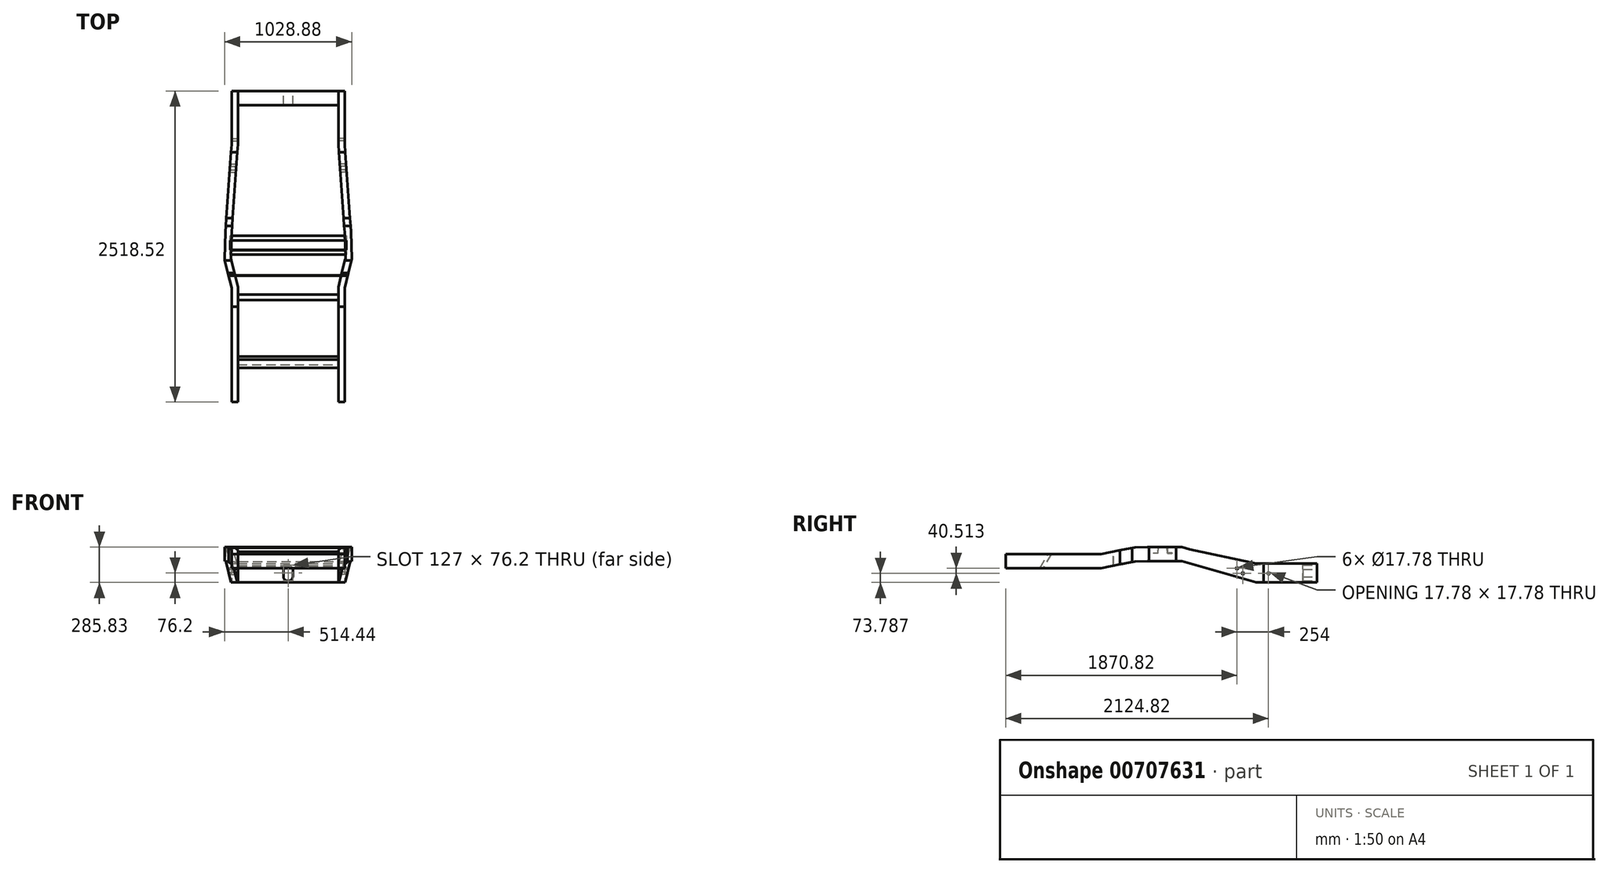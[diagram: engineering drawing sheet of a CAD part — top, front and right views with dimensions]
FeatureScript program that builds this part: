
annotation { "Feature Type Name" : "Feature", "Feature Type Description" : "" }
export const myFeature = defineFeature(function(context is Context, id is Id, definition is map)
    precondition{}
    {
        {
            var Q0;
            Q0=qCreatedBy(makeId("Top.planeOp"),FACE);
            var sketch = newSketch(context, id + "F0", { "sketchPlane" : qUnion([Q0])});
            skLineSegment(sketch, "E0", {"start": v(0, 1936.1) * mm, "end": v(0, -5906.31) * mm, "construction": true});
            skLineSegment(sketch, "E1", {"start": v(431.8, 0) * mm, "end": v(431.8, -431.8) * mm});
            skLineSegment(sketch, "E2", {"start": v(431.8, -431.8) * mm, "end": v(482.6, -1141.18) * mm});
            skLineSegment(sketch, "E3", {"start": v(482.6, -1141.18) * mm, "end": v(488.95, -1356.99) * mm});
            skLineSegment(sketch, "E4", {"start": v(488.95, -1356.99) * mm, "end": v(431.8, -1591.42) * mm});
            skLineSegment(sketch, "E5", {"start": v(431.8, -1591.42) * mm, "end": v(431.8, -2518.52) * mm});
            skLineSegment(sketch, "E6", {"start": v(431.8, -431.8) * mm, "end": v(431.8, -1285.92) * mm, "construction": true});
            skSolve(sketch);
        }
        {
            var Q0;
            Q0=qCreatedBy(makeId("Front.planeOp"),FACE);
            var Q1;
            Q1=sQuery(id+"F0.wireOp",VERTEX,"E1.start");
            cPlane(context, id + "F1", {"entities" : qUnion([Q0, Q1]), "cplaneType" : CPlaneType.PLANE_POINT, "offset" : 25.4 * mm, "width" : 152.4 * mm, "height" : 152.4 * mm});
        }
        {
            var Q0;
            Q0=qCreatedBy(id+"F1.planeOp",FACE);
            var sketch = newSketch(context, id + "F2", { "sketchPlane" : qUnion([Q0])});
            skLineSegment(sketch, "E7.bottom", {"start": v(406.4, 203.2) * mm, "end": v(457.2, 203.2) * mm});
            skLineSegment(sketch, "E7.top", {"start": v(406.4, -203.2) * mm, "end": v(457.2, -203.2) * mm});
            skLineSegment(sketch, "E7.left", {"start": v(406.4, 203.2) * mm, "end": v(406.4, -203.2) * mm});
            skLineSegment(sketch, "E7.right", {"start": v(457.2, 203.2) * mm, "end": v(457.2, -203.2) * mm});
            skPoint(sketch, "E7.middle", {"position": v(431.8, 0) * mm});
            skLineSegment(sketch, "E8", {"start": v(0, 0) * mm, "end": v(572.75, 0) * mm, "construction": true});
            skSolve(sketch);
        }
        {
            var Q0;
            Q0=qSketchRegion(id+"F2",true);
            var Q1;
            Q1=qConstructionFilter(qBodyType(qCreatedBy(id+"F0",EDGE),BodyType.WIRE),ConstructionObject.NO);
            sweep(context, id + "F3", {"profiles" : qUnion([Q0]), "path" : qUnion([Q1])});
        }
        {
            var Q0;
            Q0=qCreatedBy(makeId("Right.planeOp"),FACE);
            var sketch = newSketch(context, id + "F4", { "sketchPlane" : qUnion([Q0])});
            skLineSegment(sketch, "E9", {"start": v(0, -203.2) * mm, "end": v(-493.71, -203.2) * mm});
            skLineSegment(sketch, "E10", {"start": v(-493.71, -203.2) * mm, "end": v(-1091.9, -31.67) * mm});
            skLineSegment(sketch, "E11", {"start": v(-1091.9, -31.67) * mm, "end": v(-1371.3, -31.67) * mm});
            skLineSegment(sketch, "E12", {"start": v(-1371.3, -31.67) * mm, "end": v(-1472.9, -33.44) * mm});
            skLineSegment(sketch, "E13", {"start": v(-1371.3, -31.67) * mm, "end": v(-1529.34, -31.67) * mm, "construction": true});
            skLineSegment(sketch, "E14", {"start": v(-1472.9, -33.44) * mm, "end": v(-1747.16, -86.76) * mm});
            skLineSegment(sketch, "E15", {"start": v(-1747.16, -86.76) * mm, "end": v(-2518.52, -86.76) * mm});
            skLineSegment(sketch, "E16", {"start": v(-2518.52, -86.76) * mm, "end": v(-2518.52, -253.61) * mm});
            skLineSegment(sketch, "E17", {"start": v(-2518.52, -253.61) * mm, "end": v(0, -269.23) * mm});
            skLineSegment(sketch, "E18", {"start": v(0, -269.23) * mm, "end": v(0, -203.2) * mm});
            skLineSegment(sketch, "E19", {"start": v(0, -50.8) * mm, "end": v(-493.71, -50.8) * mm});
            skLineSegment(sketch, "E20", {"start": v(-493.71, -50.8) * mm, "end": v(-1028.7, 64.5) * mm});
            skLineSegment(sketch, "E21", {"start": v(-1028.7, 64.5) * mm, "end": v(-1028.7, -49.8) * mm, "construction": true});
            skLineSegment(sketch, "E22", {"start": v(-1091.9, -31.67) * mm, "end": v(-1091.9, 82.63) * mm, "construction": true});
            skLineSegment(sketch, "E23", {"start": v(-1371.3, -31.67) * mm, "end": v(-1371.3, 82.63) * mm, "construction": true});
            skLineSegment(sketch, "E24", {"start": v(-1472.9, -33.44) * mm, "end": v(-1472.9, 80.86) * mm, "construction": true});
            skLineSegment(sketch, "E25", {"start": v(-1747.16, -86.76) * mm, "end": v(-1747.16, 27.54) * mm, "construction": true});
            skLineSegment(sketch, "E26", {"start": v(-1028.7, 64.5) * mm, "end": v(-1091.9, 82.63) * mm});
            skLineSegment(sketch, "E27", {"start": v(-1091.9, 82.63) * mm, "end": v(-1371.3, 82.63) * mm});
            skLineSegment(sketch, "E28", {"start": v(-1472.9, 80.86) * mm, "end": v(-1747.16, 27.54) * mm});
            skLineSegment(sketch, "E29", {"start": v(-1472.9, 80.86) * mm, "end": v(-1371.3, 82.63) * mm});
            skLineSegment(sketch, "E30", {"start": v(-2518.52, -86.76) * mm, "end": v(-2518.52, 27.54) * mm, "construction": true});
            skLineSegment(sketch, "E31", {"start": v(-1747.16, 27.54) * mm, "end": v(-2518.52, 27.54) * mm});
            skLineSegment(sketch, "E32", {"start": v(-2518.52, 27.54) * mm, "end": v(-2518.52, 524.74) * mm});
            skLineSegment(sketch, "E33", {"start": v(-2518.52, 524.74) * mm, "end": v(0, 524.74) * mm});
            skLineSegment(sketch, "E34", {"start": v(0, 524.74) * mm, "end": v(0, -50.8) * mm});
            skSolve(sketch);
        }
        {
            var Q0;
            Q0=qSketchRegion(id+"F4",true);
            var Q1;
            Q1=makeQuery(id+"F3.opSweep","SWEPT_FACE",FACE,{"disambiguationData":[OSD([sQuery(id+"F0.wireOp",EDGE,"1umSsKEu-dJId-BIwL-yde3-wRK5SwyTBX2N"),sQuery(id+"F2.wireOp",EDGE,"E7.right")])]});
            extrude(context, id + "F5", {"entities" : qUnion([Q0]), "operationType" : NewBodyOperationType.REMOVE, "depth" : 609.6 * mm, "endBoundEntityFace" : qUnion([Q1]), "offsetDistance" : 25.4 * mm});
        }
        {
            var Q0;
            Q0=makeQuery(id+"F3.opSweep","SWEPT_FACE",FACE,{"disambiguationData":[OSD([sQuery(id+"F0.wireOp",EDGE,"E1"),sQuery(id+"F2.wireOp",EDGE,"E7.left")])]});
            var sketch = newSketch(context, id + "F6", { "sketchPlane" : qUnion([Q0])});
            skLineSegment(sketch, "E35", {"start": v(-416.37, -129.41) * mm, "end": v(600.08, -129.41) * mm, "construction": true});
            skLineSegment(sketch, "E36", {"start": v(393.7, 39.46) * mm, "end": v(393.7, -270.74) * mm, "construction": true});
            skLineSegment(sketch, "E37", {"start": v(393.7, -88.9) * mm, "end": v(863.06, -88.9) * mm, "construction": true});
            skLineSegment(sketch, "E38", {"start": v(600.08, 71) * mm, "end": v(600.08, -269.25) * mm, "construction": true});
            skLineSegment(sketch, "E39", {"start": v(647.7, 77.42) * mm, "end": v(647.7, -282.1) * mm, "construction": true});
            skCircle(sketch, "E40", {"center": v(600.08, -129.41) * mm, "radius": 8.9 * mm});
            skCircle(sketch, "E41", {"center": v(647.7, -88.9) * mm, "radius": 8.9 * mm});
            skCircle(sketch, "E42", {"center": v(393.7, -129.41) * mm, "radius": 8.9 * mm});
            skSolve(sketch);
        }
        {
            var Q0;
            Q0=qSketchRegion(id+"F6",true);
            extrude(context, id + "F7", {"entities" : qUnion([Q0]), "operationType" : NewBodyOperationType.REMOVE, "endBound" : BoundingType.SYMMETRIC, "oppositeDirection" : true, "depth" : 508 * mm, "offsetDistance" : 25.4 * mm});
        }
        {
            var Q0;
            Q0=makeQuery(id+"F3.opSweep","SWEPT_BODY",BODY,{"disambiguationData":[OSD([sQuery(id+"F0.wireOp",EDGE,"zRG0IsD7-SMmf-8p0A-3XBu-xbHUB45AKsED"),sQuery(id+"F2.wireOp",EDGE,"E7.bottom"),sQuery(id+"F2.wireOp",EDGE,"E7.top"),sQuery(id+"F2.wireOp",EDGE,"E7.left"),sQuery(id+"F2.wireOp",EDGE,"E7.right")])]});
            var Q1;
            Q1=qCreatedBy(makeId("Right.planeOp"),FACE);
            mirror(context, id + "F8", {"entities" : qUnion([Q0]), "mirrorPlane" : qUnion([Q1])});
        }
        {
            var Q0;
            Q0=makeQuery(id+"F3.opSweep","SWEPT_FACE",FACE,{"disambiguationData":[OSD([sQuery(id+"F0.wireOp",EDGE,"E1"),sQuery(id+"F2.wireOp",EDGE,"E7.left")])]});
            var sketch = newSketch(context, id + "F9", { "sketchPlane" : qUnion([Q0])});
            skLineSegment(sketch, "E43.bottom", {"start": v(0, -50.8) * mm, "end": v(114.3, -50.8) * mm});
            skLineSegment(sketch, "E43.top", {"start": v(0, -203.2) * mm, "end": v(114.3, -203.2) * mm});
            skLineSegment(sketch, "E43.left", {"start": v(0, -50.8) * mm, "end": v(0, -203.2) * mm});
            skLineSegment(sketch, "E43.right", {"start": v(114.3, -50.8) * mm, "end": v(114.3, -203.2) * mm});
            skSolve(sketch);
        }
        {
            var Q0;
            Q0=qSketchRegion(id+"F9",true);
            var Q1;
            Q1=makeQuery(id+"F8.opPattern","COPY",FACE,{"derivedFrom":makeQuery(id+"F3.opSweep","SWEPT_FACE",FACE,{"disambiguationData":[OSD([sQuery(id+"F0.wireOp",EDGE,"E1"),sQuery(id+"F2.wireOp",EDGE,"E7.left")])]}),"instanceName":"1"});
            extrude(context, id + "F10", {"entities" : qUnion([Q0]), "endBound" : BoundingType.UP_TO_SURFACE, "depth" : 25.4 * mm, "endBoundEntityFace" : qUnion([Q1]), "offsetDistance" : 25.4 * mm});
        }
        {
            var Q0;
            Q0=makeQuery(id+"F3.opSweep","SWEPT_FACE",FACE,{"disambiguationData":[OSD([sQuery(id+"F0.wireOp",EDGE,"E5"),sQuery(id+"F2.wireOp",EDGE,"E7.left")])]});
            var sketch = newSketch(context, id + "F11", { "sketchPlane" : qUnion([Q0])});
            skLineSegment(sketch, "E44", {"start": v(2175.62, 27.54) * mm, "end": v(2241.62, -86.76) * mm});
            skLineSegment(sketch, "E45", {"start": v(2241.62, -86.76) * mm, "end": v(2216.22, -86.76) * mm});
            skLineSegment(sketch, "E46", {"start": v(2216.22, -86.76) * mm, "end": v(2150.22, 27.54) * mm});
            skLineSegment(sketch, "E47", {"start": v(2150.22, 27.54) * mm, "end": v(2175.62, 27.54) * mm});
            skSolve(sketch);
        }
        {
            var Q0;
            Q0=qSketchRegion(id+"F11",true);
            var Q1;
            Q1=makeQuery(id+"F8.opPattern","COPY",FACE,{"derivedFrom":makeQuery(id+"F3.opSweep","SWEPT_FACE",FACE,{"disambiguationData":[OSD([sQuery(id+"F0.wireOp",EDGE,"E5"),sQuery(id+"F2.wireOp",EDGE,"E7.left")])]}),"instanceName":"1"});
            extrude(context, id + "F12", {"entities" : qUnion([Q0]), "endBound" : BoundingType.UP_TO_SURFACE, "depth" : 25.4 * mm, "endBoundEntityFace" : qUnion([Q1]), "offsetDistance" : 25.4 * mm});
        }
        {
            var Q0;
            Q0=makeQuery(id+"F3.opSweep","SWEPT_FACE",FACE,{"disambiguationData":[OSD([sQuery(id+"F0.wireOp",EDGE,"E5"),sQuery(id+"F2.wireOp",EDGE,"E7.left")])]});
            var sketch = newSketch(context, id + "F13", { "sketchPlane" : qUnion([Q0])});
            skLineSegment(sketch, "E48", {"start": v(1693.02, 38.07) * mm, "end": v(1646.27, 47.15) * mm});
            skLineSegment(sketch, "E49", {"start": v(1646.27, 47.15) * mm, "end": v(1646.27, -67.15) * mm});
            skLineSegment(sketch, "E50", {"start": v(1646.27, -67.15) * mm, "end": v(1693.02, -76.23) * mm});
            skLineSegment(sketch, "E51", {"start": v(1693.02, -76.23) * mm, "end": v(1693.02, -73.13) * mm});
            skLineSegment(sketch, "E52", {"start": v(1649.32, 43.46) * mm, "end": v(1693.02, 34.96) * mm});
            skLineSegment(sketch, "E53", {"start": v(1693.02, 34.96) * mm, "end": v(1693.02, 38.07) * mm});
            skLineSegment(sketch, "E54", {"start": v(1693.02, -73.13) * mm, "end": v(1649.32, -64.63) * mm});
            skLineSegment(sketch, "E55", {"start": v(1649.32, 43.46) * mm, "end": v(1649.32, -64.63) * mm});
            skSolve(sketch);
        }
        {
            var Q0;
            Q0=qSketchRegion(id+"F13",true);
            var Q1;
            Q1=makeQuery(id+"F8.opPattern","COPY",FACE,{"derivedFrom":makeQuery(id+"F3.opSweep","SWEPT_FACE",FACE,{"disambiguationData":[OSD([sQuery(id+"F0.wireOp",EDGE,"E5"),sQuery(id+"F2.wireOp",EDGE,"E7.left")])]}),"instanceName":"1"});
            extrude(context, id + "F14", {"entities" : qUnion([Q0]), "endBound" : BoundingType.UP_TO_SURFACE, "depth" : 25.4 * mm, "endBoundEntityFace" : qUnion([Q1]), "offsetDistance" : 25.4 * mm});
        }
        {
            var Q0;
            Q0=qCreatedBy(makeId("Right.planeOp"),FACE);
            var sketch = newSketch(context, id + "F15", { "sketchPlane" : qUnion([Q0])});
            skLineSegment(sketch, "E56", {"start": v(-1248.52, 150.62) * mm, "end": v(-1248.52, -76.38) * mm, "construction": true});
            skLineSegment(sketch, "E57", {"start": v(-1248.52, 82.63) * mm, "end": v(-1286.62, 82.63) * mm});
            skLineSegment(sketch, "E58", {"start": v(-1286.62, 82.63) * mm, "end": v(-1288.3, 34.88) * mm});
            skLineSegment(sketch, "E59", {"start": v(-1324.72, 34.88) * mm, "end": v(-1288.3, 34.88) * mm});
            skLineSegment(sketch, "E60", {"start": v(-1324.72, 34.88) * mm, "end": v(-1324.72, 31.83) * mm});
            skLineSegment(sketch, "E61", {"start": v(-1285.35, 31.83) * mm, "end": v(-1324.72, 31.83) * mm});
            skLineSegment(sketch, "E62", {"start": v(-1285.35, 31.83) * mm, "end": v(-1283.68, 79.58) * mm});
            skLineSegment(sketch, "E63", {"start": v(-1283.68, 79.58) * mm, "end": v(-1248.52, 79.58) * mm});
            skLineSegment(sketch, "E64.MirrorCS", {"start": v(-1172.32, 34.88) * mm, "end": v(-1172.32, 31.83) * mm});
            skLineSegment(sketch, "E65.MirrorCS", {"start": v(-1211.7, 31.83) * mm, "end": v(-1172.32, 31.83) * mm});
            skLineSegment(sketch, "E66.MirrorCS", {"start": v(-1172.32, 34.88) * mm, "end": v(-1208.76, 34.88) * mm});
            skLineSegment(sketch, "E67.MirrorCS", {"start": v(-1210.42, 82.63) * mm, "end": v(-1208.76, 34.88) * mm});
            skLineSegment(sketch, "E68.MirrorCS", {"start": v(-1211.7, 31.83) * mm, "end": v(-1213.37, 79.58) * mm});
            skLineSegment(sketch, "E69.MirrorCS", {"start": v(-1248.52, 82.63) * mm, "end": v(-1210.42, 82.63) * mm});
            skLineSegment(sketch, "E70.MirrorCS", {"start": v(-1213.37, 79.58) * mm, "end": v(-1248.52, 79.58) * mm});
            skSolve(sketch);
        }
        {
            var Q0;
            Q0=qSketchRegion(id+"F15",true);
            extrude(context, id + "F16", {"entities" : qUnion([Q0]), "endBound" : BoundingType.SYMMETRIC, "depth" : 939.8 * mm, "offsetDistance" : 25.4 * mm});
        }
        {
            var Q0;
            Q0=makeQuery(id+"F10.opExtrude","SWEPT_FACE",FACE,{"disambiguationData":[OSD([sQuery(id+"F9.wireOp",EDGE,"E43.left")])]});
            var sketch = newSketch(context, id + "F17", { "sketchPlane" : qUnion([Q0])});
            skLineSegment(sketch, "E71", {"start": v(0, -50.8) * mm, "end": v(0, -203.2) * mm, "construction": true});
            skLineSegment(sketch, "E72", {"start": v(-55.42, -127) * mm, "end": v(70.2, -127) * mm, "construction": true});
            skPoint(sketch, "E72.startSnap0", {"position": v(0, -127) * mm});
            skArc(sketch, "E73", {"start": v(38.1, -97.33) * mm, "mid": v(0, -63.5) * mm, "end": v(-38.1, -97.33) * mm});
            skArc(sketch, "E74.MirrorC", {"start": v(38.1, -156.67) * mm, "mid": v(0, -190.5) * mm, "end": v(-38.1, -156.67) * mm});
            skLineSegment(sketch, "E75", {"start": v(-38.1, -97.33) * mm, "end": v(-38.1, -156.67) * mm});
            skLineSegment(sketch, "E76.MirrorCS", {"start": v(38.1, -97.33) * mm, "end": v(38.1, -156.67) * mm});
            skSolve(sketch);
        }
        {
            var Q0;
            Q0=qSketchRegion(id+"F17",true);
            var Q1;
            Q1=makeQuery(id+"F10.opExtrude","SWEPT_FACE",FACE,{"disambiguationData":[OSD([sQuery(id+"F9.wireOp",EDGE,"E43.right")])]});
            extrude(context, id + "F18", {"entities" : qUnion([Q0]), "operationType" : NewBodyOperationType.REMOVE, "endBound" : BoundingType.UP_TO_SURFACE, "oppositeDirection" : true, "depth" : 25.4 * mm, "endBoundEntityFace" : qUnion([Q1]), "offsetDistance" : 25.4 * mm});
        }
        {
            var Q0;
            Q0=makeQuery(id+"F8.opPattern","COPY",FACE,{"derivedFrom":makeQuery(id+"F3.opSweep","CAP_FACE",FACE,{"disambiguationData":[OSD([sQuery(id+"F0.wireOp",VERTEX,"E5.end"),sQuery(id+"F2.wireOp",EDGE,"E7.bottom"),sQuery(id+"F2.wireOp",EDGE,"E7.top"),sQuery(id+"F2.wireOp",EDGE,"E7.left"),sQuery(id+"F2.wireOp",EDGE,"E7.right")])],"isStart":false}),"instanceName":"1"});
            cPlane(context, id + "F19", {"entities" : qUnion([Q0]), "cplaneType" : CPlaneType.OFFSET, "offset" : 1022.35 * mm, "oppositeDirection" : true, "width" : 152.4 * mm, "height" : 152.4 * mm});
        }
        {
            var Q0;
            Q0=qCreatedBy(id+"F19.planeOp",FACE);
            var sketch = newSketch(context, id + "F20", { "sketchPlane" : qUnion([Q0])});
            skLineSegment(sketch, "E77", {"start": v(-481.16, 76.33) * mm, "end": v(481.16, 76.33) * mm});
            skLineSegment(sketch, "E78", {"start": v(481.16, 76.33) * mm, "end": v(481.16, -37.97) * mm});
            skLineSegment(sketch, "E79", {"start": v(481.16, -37.97) * mm, "end": v(-481.16, -37.97) * mm});
            skLineSegment(sketch, "E80", {"start": v(-481.16, -37.97) * mm, "end": v(-481.16, 76.33) * mm});
            skSolve(sketch);
        }
        {
            var Q0;
            Q0=qSketchRegion(id+"F20",true);
            extrude(context, id + "F21", {"entities" : qUnion([Q0]), "oppositeDirection" : true, "depth" : 4.76 * mm, "offsetDistance" : 25.4 * mm});
        }
    });
